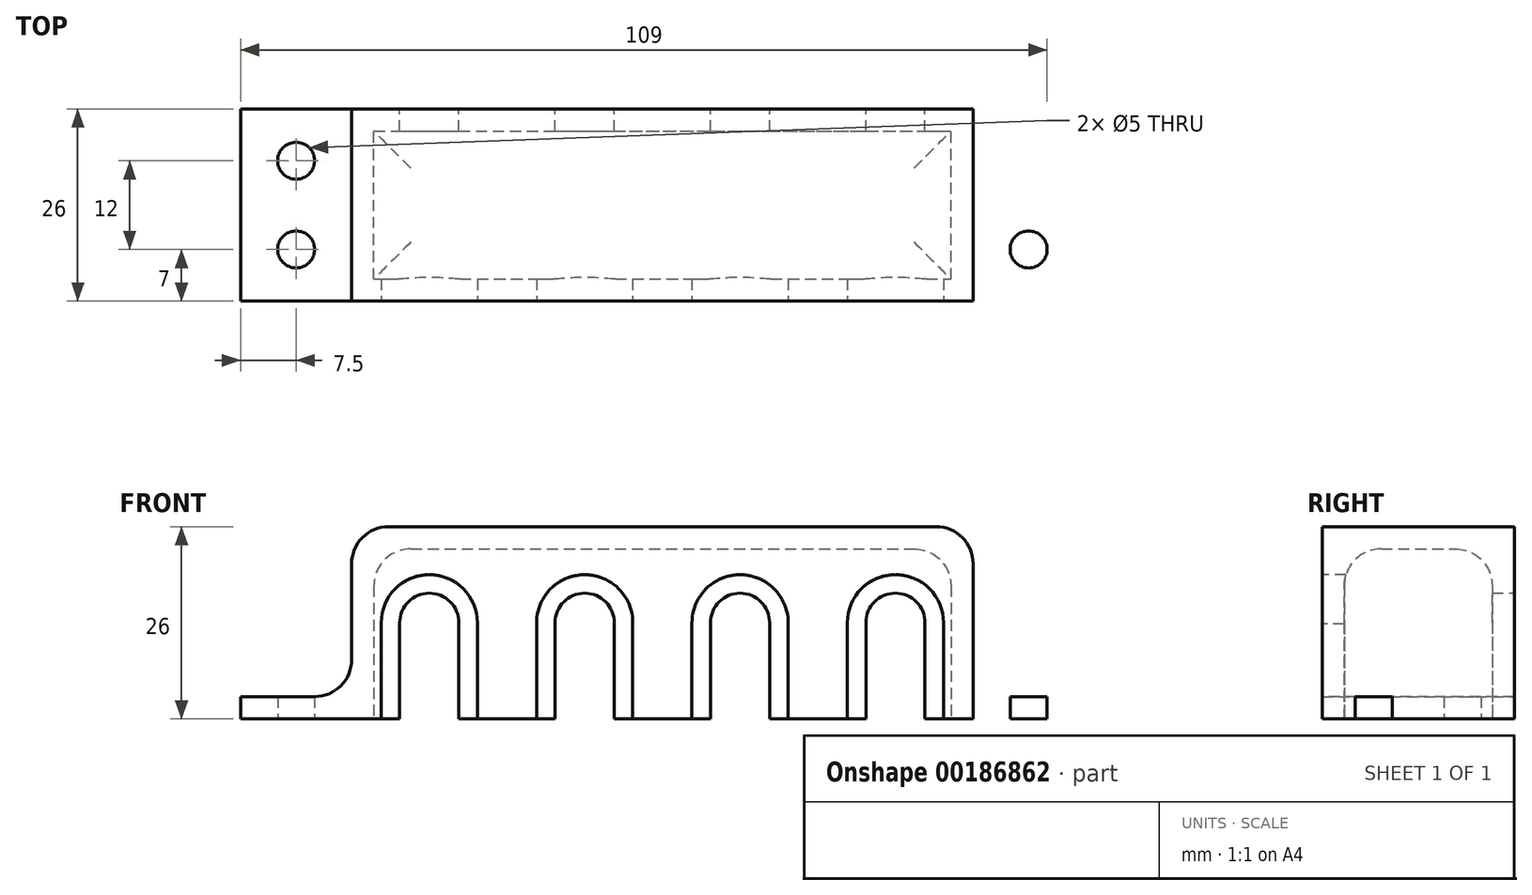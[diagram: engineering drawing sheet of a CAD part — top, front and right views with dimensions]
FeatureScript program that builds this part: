
annotation { "Feature Type Name" : "Feature", "Feature Type Description" : "" }
export const myFeature = defineFeature(function(context is Context, id is Id, definition is map)
    precondition{}
    {
        {
            var Q0;
            Q0=qCreatedBy(makeId("Front.planeOp"),FACE);
            var sketch = newSketch(context, id + "F0", { "sketchPlane" : qUnion([Q0])});
            skLineSegment(sketch, "E0.bottom", {"start": v(-42, 11) * mm, "end": v(42, 11) * mm});
            skLineSegment(sketch, "E0.top", {"start": v(-42, -11) * mm, "end": v(42, -11) * mm});
            skLineSegment(sketch, "E0.left", {"start": v(-42, 11) * mm, "end": v(-42, -11) * mm});
            skLineSegment(sketch, "E0.right", {"start": v(42, 11) * mm, "end": v(42, -11) * mm});
            skPoint(sketch, "E0.middle", {"position": v(0, 0) * mm});
            skCircle(sketch, "E1", {"center": v(-10.5, 0) * mm, "radius": 6.5 * mm});
            skCircle(sketch, "E2", {"center": v(-31.5, 0) * mm, "radius": 6.5 * mm});
            skCircle(sketch, "E3.MirrorC", {"center": v(10.5, 0) * mm, "radius": 6.5 * mm});
            skCircle(sketch, "E4.MirrorC", {"center": v(31.5, 0) * mm, "radius": 6.5 * mm});
            skSolve(sketch);
        }
        {
            var Q0;
            Q0=qCreatedBy(makeId("Top.planeOp"),FACE);
            var sketch = newSketch(context, id + "F1", { "sketchPlane" : qUnion([Q0])});
            skPoint(sketch, "E5.0", {"position": v(-42, 0) * mm});
            skPoint(sketch, "E6.0", {"position": v(42, 0) * mm});
            skLineSegment(sketch, "E7.bottom", {"start": v(-42, 0) * mm, "end": v(42, 0) * mm});
            skLineSegment(sketch, "E7.top", {"start": v(-42, 26) * mm, "end": v(42, 26) * mm});
            skLineSegment(sketch, "E7.left", {"start": v(-42, 0) * mm, "end": v(-42, 26) * mm});
            skLineSegment(sketch, "E7.right", {"start": v(42, 0) * mm, "end": v(42, 26) * mm});
            skSolve(sketch);
        }
        {
            var Q0;
            Q0 = qSketchRegion(id + "F1", true);
            extrude(context, id + "F2", {"entities" : qUnion([Q0]), "depth" : 13 * mm, "offsetDistance" : 25 * mm, "hasSecondDirection" : true, "secondDirectionOppositeDirection" : true, "secondDirectionDepth" : 13 * mm});
        }
        {
            var Q0;
            Q0=makeQuery(id+"F2.opExtrude","CAP_FACE",FACE,{"disambiguationData":[OSD([sQuery(id+"F1.wireOp",EDGE,"E7.bottom"),sQuery(id+"F1.wireOp",EDGE,"E7.top"),sQuery(id+"F1.wireOp",EDGE,"E7.left"),sQuery(id+"F1.wireOp",EDGE,"E7.right")])],"isStart":true});
            shell(context, id + "F3", {"entities" : qUnion([Q0]), "thickness" : 3 * mm});
        }
        {
            var Q0;
            Q0=makeQuery(id+"F2.opExtrude","SWEPT_FACE",FACE,{"disambiguationData":[OSD([sQuery(id+"F1.wireOp",EDGE,"E7.top")])]});
            var sketch = newSketch(context, id + "F4", { "sketchPlane" : qUnion([Q0])});
            skPoint(sketch, "E8.0", {"position": v(-31.5, 0) * mm});
            skPoint(sketch, "E9.0", {"position": v(-10.5, 0) * mm});
            skPoint(sketch, "E10.0", {"position": v(10.5, 0) * mm});
            skPoint(sketch, "E11.0", {"position": v(31.5, 0) * mm});
            skPoint(sketch, "E12.center.orphan", {"position": v(-23, 0) * mm});
            skArc(sketch, "E13", {"start": v(-6.5, 0) * mm, "mid": v(-10.5, 4) * mm, "end": v(-14.5, 0) * mm});
            skArc(sketch, "E14", {"start": v(-27.5, 0) * mm, "mid": v(-31.5, 4) * mm, "end": v(-35.5, 0) * mm});
            skArc(sketch, "E15.MirrorC", {"start": v(6.5, 0) * mm, "mid": v(10.5, 4) * mm, "end": v(14.5, 0) * mm});
            skArc(sketch, "E16.MirrorC", {"start": v(27.5, 0) * mm, "mid": v(31.5, 4) * mm, "end": v(35.5, 0) * mm});
            skLineSegment(sketch, "E17", {"start": v(-35.5, 0) * mm, "end": v(-35.5, -13) * mm});
            skLineSegment(sketch, "E18", {"start": v(-27.5, 0) * mm, "end": v(-27.5, -13) * mm});
            skLineSegment(sketch, "E19", {"start": v(-14.5, 0) * mm, "end": v(-14.5, -13) * mm});
            skLineSegment(sketch, "E20", {"start": v(-6.5, 0) * mm, "end": v(-6.5, -13) * mm});
            skLineSegment(sketch, "E21.MirrorCS", {"start": v(6.5, 0) * mm, "end": v(6.5, -13) * mm});
            skLineSegment(sketch, "E22.MirrorCS", {"start": v(14.5, 0) * mm, "end": v(14.5, -13) * mm});
            skLineSegment(sketch, "E23.MirrorCS", {"start": v(27.5, 0) * mm, "end": v(27.5, -13) * mm});
            skLineSegment(sketch, "E24.MirrorCS", {"start": v(35.5, 0) * mm, "end": v(35.5, -13) * mm});
            skLineSegment(sketch, "E25", {"start": v(-35.5, -13) * mm, "end": v(-27.5, -13) * mm});
            skLineSegment(sketch, "E26", {"start": v(-14.5, -13) * mm, "end": v(-6.5, -13) * mm});
            skLineSegment(sketch, "E27", {"start": v(6.5, -13) * mm, "end": v(14.5, -13) * mm});
            skLineSegment(sketch, "E28", {"start": v(27.5, -13) * mm, "end": v(35.5, -13) * mm});
            skSolve(sketch);
        }
        {
            var Q0;
            Q0=makeQuery(id+"F2.opExtrude","CAP_FACE",FACE,{"disambiguationData":[OSD([sQuery(id+"F1.wireOp",EDGE,"E7.bottom"),sQuery(id+"F1.wireOp",EDGE,"E7.top"),sQuery(id+"F1.wireOp",EDGE,"E7.left"),sQuery(id+"F1.wireOp",EDGE,"E7.right")])],"isStart":true});
            var sketch = newSketch(context, id + "F5", { "sketchPlane" : qUnion([Q0])});
            skLineSegment(sketch, "E29.bottom", {"start": v(-42, 0) * mm, "end": v(-57, 0) * mm});
            skLineSegment(sketch, "E29.top", {"start": v(-42, -26) * mm, "end": v(-57, -26) * mm});
            skLineSegment(sketch, "E29.left", {"start": v(-42, 0) * mm, "end": v(-42, -26) * mm});
            skLineSegment(sketch, "E29.right", {"start": v(-57, 0) * mm, "end": v(-57, -26) * mm});
            skLineSegment(sketch, "E30", {"start": v(-49.5, 0) * mm, "end": v(-49.5, -26) * mm, "construction": true});
            skCircle(sketch, "E31", {"center": v(-49.5, -7) * mm, "radius": 2.5 * mm});
            skLineSegment(sketch, "E32", {"start": v(-57, -13) * mm, "end": v(-42, -13) * mm, "construction": true});
            skCircle(sketch, "E33.MirrorC", {"center": v(-49.5, -19) * mm, "radius": 2.5 * mm});
            skCircle(sketch, "E34.MirrorC", {"center": v(49.5, -7) * mm, "radius": 2.5 * mm});
            skCircle(sketch, "E35.MirrorC", {"center": v(49.5, -19) * mm, "radius": 2.5 * mm});
            skLineSegment(sketch, "E36.MirrorCS", {"start": v(42, 0) * mm, "end": v(57, 0) * mm});
            skLineSegment(sketch, "E37.MirrorCS", {"start": v(57, 0) * mm, "end": v(57, -26) * mm});
            skLineSegment(sketch, "E38.MirrorCS", {"start": v(42, -26) * mm, "end": v(57, -26) * mm});
            skLineSegment(sketch, "E39.0.0", {"start": v(-42, -26) * mm, "end": v(42, -26) * mm});
            skLineSegment(sketch, "E39.0.1", {"start": v(42, -26) * mm, "end": v(42, 0) * mm});
            skLineSegment(sketch, "E39.0.2", {"start": v(42, 0) * mm, "end": v(-42, 0) * mm});
            skSolve(sketch);
        }
        {
            var Q0;
            Q0=makeQuery(id+"F5.imprint","IMPRINT",FACE,{"disambiguationData":[TD([[makeQuery(id+"F5.imprint","IMPRINT",EDGE,{"derivedFrom":sQuery(id+"F5.wireOp",EDGE,"E29.bottom")}),1.0]])]});
            var Q1;
            Q1=makeQuery(id+"F5.imprint","IMPRINT",FACE,{"disambiguationData":[TD([[makeQuery(id+"F5.imprint","IMPRINT",EDGE,{"derivedFrom":sQuery(id+"F5.wireOp",EDGE,"E39.0.0")}),1.0]])]});
            var Q2;
            Q2=makeQuery(id+"F5.imprint","IMPRINT",FACE,{"disambiguationData":[TD([[makeQuery(id+"F5.imprint","IMPRINT",EDGE,{"derivedFrom":sQuery(id+"F5.wireOp",EDGE,"E34.MirrorC")}),1.0]])]});
            extrude(context, id + "F6", {"entities" : qUnion([Q0, Q1, Q2]), "operationType" : NewBodyOperationType.ADD, "oppositeDirection" : true, "depth" : 3 * mm, "offsetDistance" : 25 * mm});
        }
        {
            var Q0;
            Q0=makeQuery(id+"F2.opExtrude","CAP_EDGE",EDGE,{"disambiguationData":[OSD([sQuery(id+"F1.wireOp",EDGE,"E7.left")])],"isStart":false});
            var Q1;
            Q1=makeQuery(id+"F2.opExtrude","CAP_EDGE",EDGE,{"disambiguationData":[OSD([sQuery(id+"F1.wireOp",EDGE,"E7.right")])],"isStart":false});
            var Q2;
            {var subQ0=sQuery(id+"F1.wireOp",EDGE,"E7.left");Q2=makeQuery(id+"F6.boolean.opBoolean","INTERSECT",EDGE,{"derivedFrom":[makeQuery(id+"F2.opExtrude","SWEPT_FACE",FACE,{"disambiguationData":[OSD([subQ0])]}),makeQuery(id+"F6.opExtrude","CAP_FACE",FACE,{"disambiguationData":[OSD([sQuery(id+"F1.wireOp",EDGE,"E7.bottom"),sQuery(id+"F1.wireOp",EDGE,"E7.top"),subQ0,sQuery(id+"F1.wireOp",EDGE,"E7.right"),sQuery(id+"F5.wireOp",EDGE,"E29.bottom"),sQuery(id+"F5.wireOp",EDGE,"E29.top"),sQuery(id+"F5.wireOp",EDGE,"E29.right"),sQuery(id+"F5.wireOp",EDGE,"E31"),sQuery(id+"F5.wireOp",EDGE,"E33.MirrorC"),sQuery(id+"F5.wireOp",EDGE,"E34.MirrorC"),sQuery(id+"F5.wireOp",EDGE,"E35.MirrorC"),sQuery(id+"F5.wireOp",EDGE,"E36.MirrorCS"),sQuery(id+"F5.wireOp",EDGE,"E37.MirrorCS"),sQuery(id+"F5.wireOp",EDGE,"E38.MirrorCS"),sQuery(id+"F5.wireOp",EDGE,"E39.0.0"),sQuery(id+"F5.wireOp",EDGE,"E39.0.2")])],"isStart":false})]});}
            var Q3;
            {var subQ0=sQuery(id+"F1.wireOp",EDGE,"E7.right");Q3=makeQuery(id+"F6.boolean.opBoolean","INTERSECT",EDGE,{"derivedFrom":[makeQuery(id+"F2.opExtrude","SWEPT_FACE",FACE,{"disambiguationData":[OSD([subQ0])]}),makeQuery(id+"F6.opExtrude","CAP_FACE",FACE,{"disambiguationData":[OSD([sQuery(id+"F1.wireOp",EDGE,"E7.bottom"),sQuery(id+"F1.wireOp",EDGE,"E7.top"),sQuery(id+"F1.wireOp",EDGE,"E7.left"),subQ0,sQuery(id+"F5.wireOp",EDGE,"E29.bottom"),sQuery(id+"F5.wireOp",EDGE,"E29.top"),sQuery(id+"F5.wireOp",EDGE,"E29.right"),sQuery(id+"F5.wireOp",EDGE,"E31"),sQuery(id+"F5.wireOp",EDGE,"E33.MirrorC"),sQuery(id+"F5.wireOp",EDGE,"E34.MirrorC"),sQuery(id+"F5.wireOp",EDGE,"E35.MirrorC"),sQuery(id+"F5.wireOp",EDGE,"E36.MirrorCS"),sQuery(id+"F5.wireOp",EDGE,"E37.MirrorCS"),sQuery(id+"F5.wireOp",EDGE,"E38.MirrorCS"),sQuery(id+"F5.wireOp",EDGE,"E39.0.0"),sQuery(id+"F5.wireOp",EDGE,"E39.0.2")])],"isStart":false})]});}
            var Q4;
            {var subQ0=sQuery(id+"F1.wireOp",EDGE,"E7.top");Q4=makeQuery(id+"F3.opShell","OFFSET_EDGE",EDGE,{"disambiguationData":[OSD([subQ0]),TDD([makeQuery(id+"F2.opExtrude","CAP_EDGE",EDGE,{"disambiguationData":[OSD([subQ0])],"isStart":false})])]});}
            var Q5;
            {var subQ0=sQuery(id+"F1.wireOp",EDGE,"E7.bottom");Q5=makeQuery(id+"F3.opShell","OFFSET_EDGE",EDGE,{"disambiguationData":[OSD([subQ0]),TDD([makeQuery(id+"F2.opExtrude","CAP_EDGE",EDGE,{"disambiguationData":[OSD([subQ0])],"isStart":false})])]});}
            var Q6;
            {var subQ0=sQuery(id+"F1.wireOp",EDGE,"E7.left");Q6=makeQuery(id+"F3.opShell","OFFSET_EDGE",EDGE,{"disambiguationData":[OSD([subQ0]),TDD([makeQuery(id+"F2.opExtrude","CAP_EDGE",EDGE,{"disambiguationData":[OSD([subQ0])],"isStart":false})])]});}
            var Q7;
            {var subQ0=sQuery(id+"F1.wireOp",EDGE,"E7.right");Q7=makeQuery(id+"F3.opShell","OFFSET_EDGE",EDGE,{"disambiguationData":[OSD([subQ0]),TDD([makeQuery(id+"F2.opExtrude","CAP_EDGE",EDGE,{"disambiguationData":[OSD([subQ0])],"isStart":false})])]});}
            fillet(context, id + "F7", {"entities" : qUnion([Q0, Q1, Q2, Q3, Q4, Q5, Q6, Q7]), "radius" : 5 * mm, "tangentPropagation" : true, "allowEdgeOverflow" : false});
        }
        {
            var Q0;
            Q0=makeQuery(id+"F0.imprint","IMPRINT",FACE,{"disambiguationData":[TD([[makeQuery(id+"F0.imprint","IMPRINT",EDGE,{"derivedFrom":sQuery(id+"F0.wireOp",EDGE,"E0.bottom")}),-1.0]])]});
            var sketch = newSketch(context, id + "F8", { "sketchPlane" : qUnion([Q0])});
            skArc(sketch, "E40.0", {"start": v(-25, 0) * mm, "mid": v(-31.5, 6.5) * mm, "end": v(-38, 0) * mm});
            skArc(sketch, "E41.0", {"start": v(-4, -0.03) * mm, "mid": v(-10.56, 6.5) * mm, "end": v(-17, -0.15) * mm});
            skArc(sketch, "E42.0", {"start": v(4, -0.03) * mm, "mid": v(10.56, 6.5) * mm, "end": v(17, -0.15) * mm});
            skArc(sketch, "E43.0", {"start": v(25, 0) * mm, "mid": v(31.5, 6.5) * mm, "end": v(38, 0) * mm});
            skLineSegment(sketch, "E44", {"start": v(-38, 0) * mm, "end": v(-38, -11) * mm});
            skLineSegment(sketch, "E45", {"start": v(-25, 0) * mm, "end": v(-25, -11) * mm});
            skLineSegment(sketch, "E46", {"start": v(-17, -0.15) * mm, "end": v(-17, -10.98) * mm});
            skLineSegment(sketch, "E47", {"start": v(-4, 0.03) * mm, "end": v(-4, -11) * mm});
            skLineSegment(sketch, "E48.MirrorCS", {"start": v(4, 0.03) * mm, "end": v(4, -11) * mm});
            skLineSegment(sketch, "E49.MirrorCS", {"start": v(17, -0.15) * mm, "end": v(17, -10.98) * mm});
            skLineSegment(sketch, "E50.MirrorCS", {"start": v(25, 0) * mm, "end": v(25, -11) * mm});
            skLineSegment(sketch, "E51.MirrorCS", {"start": v(38, 0) * mm, "end": v(38, -11) * mm});
            skPoint(sketch, "E52.orphan", {"position": v(-42, -11) * mm});
            skPoint(sketch, "E53.orphan", {"position": v(42, -11) * mm});
            skLineSegment(sketch, "E54", {"start": v(-38, -11) * mm, "end": v(-38, -13) * mm});
            skLineSegment(sketch, "E55", {"start": v(-38, -13) * mm, "end": v(-25, -13) * mm});
            skLineSegment(sketch, "E56", {"start": v(-25, -13) * mm, "end": v(-25, -11) * mm});
            skLineSegment(sketch, "E57", {"start": v(-17, -10.98) * mm, "end": v(-17, -13) * mm});
            skLineSegment(sketch, "E58", {"start": v(-17, -13) * mm, "end": v(-4, -13) * mm});
            skLineSegment(sketch, "E59", {"start": v(-4, -13) * mm, "end": v(-4, -11) * mm});
            skLineSegment(sketch, "E60.MirrorCS", {"start": v(4, -13) * mm, "end": v(4, -11) * mm});
            skLineSegment(sketch, "E61.MirrorCS", {"start": v(17, -10.98) * mm, "end": v(17, -13) * mm});
            skLineSegment(sketch, "E62.MirrorCS", {"start": v(17, -13) * mm, "end": v(4, -13) * mm});
            skLineSegment(sketch, "E63.MirrorCS", {"start": v(25, -13) * mm, "end": v(25, -11) * mm});
            skLineSegment(sketch, "E64.MirrorCS", {"start": v(38, -13) * mm, "end": v(25, -13) * mm});
            skLineSegment(sketch, "E65.MirrorCS", {"start": v(38, -11) * mm, "end": v(38, -13) * mm});
            skSolve(sketch);
        }
        {
            var Q0;
            Q0 = qSketchRegion(id + "F8", true);
            extrude(context, id + "F9", {"entities" : qUnion([Q0]), "operationType" : NewBodyOperationType.REMOVE, "oppositeDirection" : true, "depth" : 5 * mm, "offsetDistance" : 25 * mm});
        }
        {
            var Q0;
            Q0 = qSketchRegion(id + "F4", true);
            extrude(context, id + "F10", {"entities" : qUnion([Q0]), "operationType" : NewBodyOperationType.REMOVE, "oppositeDirection" : true, "depth" : 25 * mm, "offsetDistance" : 25 * mm});
        }
    });
